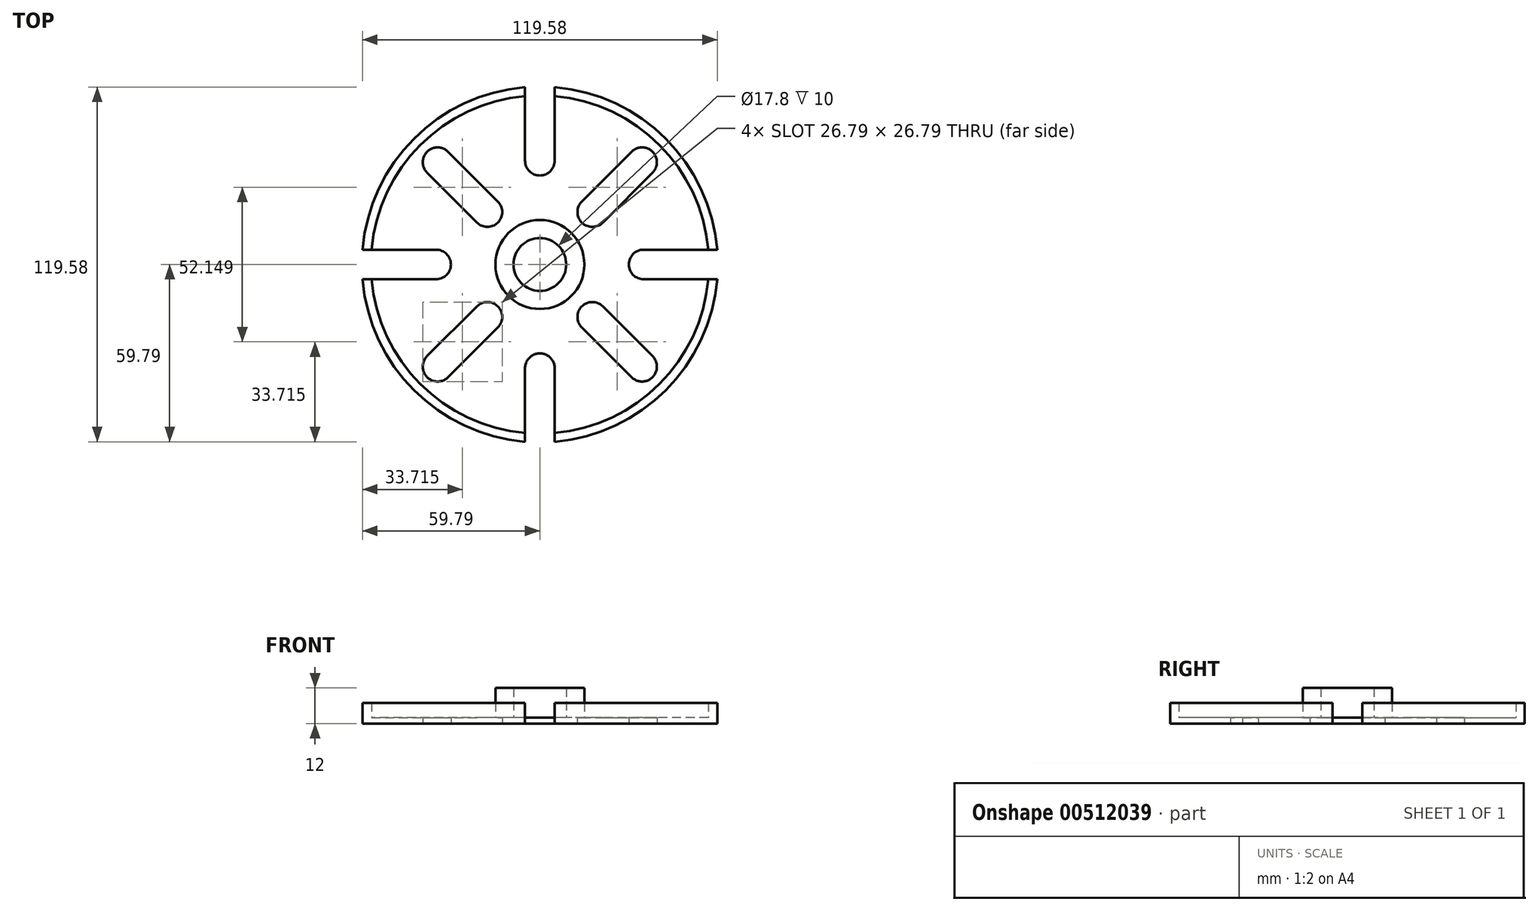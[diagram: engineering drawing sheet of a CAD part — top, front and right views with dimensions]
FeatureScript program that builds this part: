
annotation { "Feature Type Name" : "Feature", "Feature Type Description" : "" }
export const myFeature = defineFeature(function(context is Context, id is Id, definition is map)
    precondition{}
    {
        {
            var Q0;
            Q0=qCreatedBy(makeId("Top.planeOp"),FACE);
            var sketch = newSketch(context, id + "F0", { "sketchPlane" : qUnion([Q0])});
            skCircle(sketch, "E0", {"center": v(0, 0) * mm, "radius": 60 * mm});
            skLineSegment(sketch, "E1", {"start": v(0, 70.03) * mm, "end": v(0, -69.44) * mm, "construction": true});
            skLineSegment(sketch, "E2", {"start": v(57.86, 57.86) * mm, "end": v(-61.51, -61.51) * mm, "construction": true});
            skLineSegment(sketch, "E3", {"start": v(-61.51, 61.51) * mm, "end": v(64.66, -64.66) * mm, "construction": true});
            skCircle(sketch, "E4", {"center": v(0, 0) * mm, "radius": 8.9 * mm});
            skCircle(sketch, "E5", {"center": v(0, 0) * mm, "radius": 15 * mm});
            skLineSegment(sketch, "E6", {"start": v(-59.8, 5) * mm, "end": v(-29.22, 5) * mm});
            skLineSegment(sketch, "E7", {"start": v(52.5, 5) * mm, "end": v(52.5, 0) * mm, "construction": true});
            skLineSegment(sketch, "E8", {"start": v(5, 68.05) * mm, "end": v(0, 68.05) * mm, "construction": true});
            skLineSegment(sketch, "E9", {"start": v(0, 68.05) * mm, "end": v(-5, 68.05) * mm, "construction": true});
            skLineSegment(sketch, "E10", {"start": v(9.76, 16.83) * mm, "end": v(35.2, 42.26) * mm});
            skLineSegment(sketch, "E11", {"start": v(41.96, 34.9) * mm, "end": v(16.3, 9.24) * mm});
            skLineSegment(sketch, "E12", {"start": v(25.46, 32.53) * mm, "end": v(29, 29) * mm, "construction": true});
            skLineSegment(sketch, "E13", {"start": v(29, 29) * mm, "end": v(32.53, 25.46) * mm, "construction": true});
            skLineSegment(sketch, "E14", {"start": v(-35.18, 42.25) * mm, "end": v(-8.95, 16.02) * mm});
            skLineSegment(sketch, "E15", {"start": v(-8.95, 16.02) * mm, "end": v(-12.49, 12.49) * mm, "construction": true});
            skLineSegment(sketch, "E16", {"start": v(-12.49, 12.49) * mm, "end": v(-16.02, 8.95) * mm, "construction": true});
            skLineSegment(sketch, "E17", {"start": v(-16.02, 8.95) * mm, "end": v(-42.44, 35.37) * mm});
            skCircle(sketch, "E18", {"center": v(0, 0) * mm, "radius": 48.75 * mm, "construction": true});
            skCircle(sketch, "E19", {"center": v(-34.47, 34.47) * mm, "radius": 5 * mm});
            skCircle(sketch, "E20", {"center": v(34.47, 34.47) * mm, "radius": 5 * mm});
            skCircle(sketch, "E21", {"center": v(34.47, -34.47) * mm, "radius": 5 * mm});
            skCircle(sketch, "E22", {"center": v(-34.47, -34.47) * mm, "radius": 5 * mm});
            skCircle(sketch, "E23", {"center": v(0, 0) * mm, "radius": 25 * mm, "construction": true});
            skCircle(sketch, "E24", {"center": v(17.68, 17.68) * mm, "radius": 5 * mm});
            skCircle(sketch, "E25", {"center": v(17.68, -17.68) * mm, "radius": 5 * mm});
            skCircle(sketch, "E26", {"center": v(-17.68, -17.68) * mm, "radius": 5 * mm});
            skCircle(sketch, "E27", {"center": v(0, 0) * mm, "radius": 35 * mm, "construction": true});
            skCircle(sketch, "E28", {"center": v(0, 35) * mm, "radius": 5 * mm});
            skCircle(sketch, "E29", {"center": v(35, 0) * mm, "radius": 5 * mm});
            skCircle(sketch, "E30", {"center": v(0, -35) * mm, "radius": 5.01 * mm});
            skCircle(sketch, "E31", {"center": v(-35, 0) * mm, "radius": 5 * mm});
            skCircle(sketch, "E32", {"center": v(-17.68, 17.68) * mm, "radius": 5 * mm});
            skCircle(sketch, "E33", {"center": v(0, 0) * mm, "radius": 57 * mm});
            skLineSegment(sketch, "E34", {"start": v(-59.8, -5) * mm, "end": v(-29.22, -5) * mm});
            skLineSegment(sketch, "E35", {"start": v(59.8, 5) * mm, "end": v(35, 5) * mm});
            skLineSegment(sketch, "E36", {"start": v(59.8, -5) * mm, "end": v(35, -5) * mm});
            skLineSegment(sketch, "E37", {"start": v(52.5, -5) * mm, "end": v(52.5, 0) * mm, "construction": true});
            skLineSegment(sketch, "E38", {"start": v(-38, -30.94) * mm, "end": v(-17.52, -10.45) * mm});
            skLineSegment(sketch, "E39", {"start": v(-8.7, -15.76) * mm, "end": v(-33.57, -40.64) * mm});
            skLineSegment(sketch, "E40", {"start": v(-30.59, -23.52) * mm, "end": v(-27.05, -27.05) * mm, "construction": true});
            skLineSegment(sketch, "E41", {"start": v(-27.05, -27.05) * mm, "end": v(-23.52, -30.59) * mm, "construction": true});
            skLineSegment(sketch, "E42", {"start": v(5, 35) * mm, "end": v(5, 59.8) * mm});
            skLineSegment(sketch, "E43", {"start": v(-5, 35) * mm, "end": v(-5, 59.8) * mm});
            skLineSegment(sketch, "E44", {"start": v(5, -34.64) * mm, "end": v(5, -59.8) * mm});
            skLineSegment(sketch, "E45", {"start": v(-5, -35.36) * mm, "end": v(-5, -59.8) * mm});
            skLineSegment(sketch, "E46", {"start": v(-5, -45.3) * mm, "end": v(0, -45.3) * mm, "construction": true});
            skLineSegment(sketch, "E47", {"start": v(0, -45.3) * mm, "end": v(5, -45.3) * mm, "construction": true});
            skLineSegment(sketch, "E48", {"start": v(16.8, -9.72) * mm, "end": v(41.66, -34.58) * mm});
            skLineSegment(sketch, "E49", {"start": v(10.37, -17.44) * mm, "end": v(33.36, -40.43) * mm});
            skSolve(sketch);
        }
        {
            var Q0;
            {var subQ0=sQuery(id+"F0.wireOp",EDGE,"E35");var subQ1=sQuery(id+"F0.wireOp",EDGE,"E0");var subQ2=makeQuery(id+"F0.imprint","INTERSECT",VERTEX,{"derivedFrom":[subQ1,subQ0]});Q0=makeQuery(id+"F0.imprint","IMPRINT",FACE,{"disambiguationData":[TD([[makeQuery(id+"F0.imprint","IMPRINT",EDGE,{"disambiguationData":[TD([[subQ2,-1.0]])],"derivedFrom":subQ1}),1.0]])]});}
            var Q1;
            {var subQ0=sQuery(id+"F0.wireOp",EDGE,"E6");var subQ1=sQuery(id+"F0.wireOp",EDGE,"E0");var subQ2=makeQuery(id+"F0.imprint","INTERSECT",VERTEX,{"derivedFrom":[subQ1,subQ0]});Q1=makeQuery(id+"F0.imprint","IMPRINT",FACE,{"disambiguationData":[TD([[makeQuery(id+"F0.imprint","IMPRINT",EDGE,{"disambiguationData":[TD([[subQ2,1.0]])],"derivedFrom":subQ1}),1.0]])]});}
            var Q2;
            {var subQ0=sQuery(id+"F0.wireOp",EDGE,"E34");var subQ1=sQuery(id+"F0.wireOp",EDGE,"E0");var subQ2=makeQuery(id+"F0.imprint","INTERSECT",VERTEX,{"derivedFrom":[subQ1,subQ0]});Q2=makeQuery(id+"F0.imprint","IMPRINT",FACE,{"disambiguationData":[TD([[makeQuery(id+"F0.imprint","IMPRINT",EDGE,{"disambiguationData":[TD([[subQ2,-1.0]])],"derivedFrom":subQ1}),1.0]])]});}
            var Q3;
            {var subQ0=sQuery(id+"F0.wireOp",EDGE,"E36");var subQ1=sQuery(id+"F0.wireOp",EDGE,"E0");var subQ2=makeQuery(id+"F0.imprint","INTERSECT",VERTEX,{"derivedFrom":[subQ1,subQ0]});Q3=makeQuery(id+"F0.imprint","IMPRINT",FACE,{"disambiguationData":[TD([[makeQuery(id+"F0.imprint","IMPRINT",EDGE,{"disambiguationData":[TD([[subQ2,1.0]])],"derivedFrom":subQ1}),1.0]])]});}
            extrude(context, id + "F1", {"entities" : qUnion([Q0, Q1, Q2, Q3]), "depth" : 5 * mm, "offsetDistance" : 25 * mm});
        }
        {
            var Q0;
            Q0=makeQuery(id+"F0.imprint","IMPRINT",FACE,{"disambiguationData":[TD([[makeQuery(id+"F0.imprint","IMPRINT",EDGE,{"derivedFrom":sQuery(id+"F0.wireOp",EDGE,"E5")}),-1.0]])]});
            var Q1;
            Q1=makeQuery(id+"F0.imprint","IMPRINT",FACE,{"disambiguationData":[TD([[makeQuery(id+"F0.imprint","IMPRINT",EDGE,{"derivedFrom":sQuery(id+"F0.wireOp",EDGE,"E4")}),-1.0]])]});
            var Q2;
            Q2=makeQuery(id+"F0.imprint","IMPRINT",FACE,{"disambiguationData":[TD([[makeQuery(id+"F0.imprint","IMPRINT",EDGE,{"derivedFrom":sQuery(id+"F0.wireOp",EDGE,"E4")}),1.0]])]});
            var Q3;
            {var subQ0=sQuery(id+"F0.wireOp",EDGE,"E6");var subQ1=sQuery(id+"F0.wireOp",EDGE,"E0");var subQ2=makeQuery(id+"F0.imprint","INTERSECT",VERTEX,{"derivedFrom":[subQ1,subQ0]});Q3=makeQuery(id+"F0.imprint","IMPRINT",FACE,{"disambiguationData":[TD([[makeQuery(id+"F0.imprint","IMPRINT",EDGE,{"disambiguationData":[TD([[subQ2,1.0]])],"derivedFrom":subQ1}),1.0]])]});}
            var Q4;
            Q4=makeQuery(id+"F1.opExtrude","CAP_FACE",FACE,{"disambiguationData":[OSD([sQuery(id+"F0.wireOp",EDGE,"E0"),sQuery(id+"F0.wireOp",EDGE,"E6"),sQuery(id+"F0.wireOp",EDGE,"E33"),sQuery(id+"F0.wireOp",EDGE,"E43")])],"isStart":false});
            var Q5;
            Q5=makeQuery(id+"F1.opExtrude","CAP_FACE",FACE,{"disambiguationData":[OSD([sQuery(id+"F0.wireOp",EDGE,"E0"),sQuery(id+"F0.wireOp",EDGE,"E33"),sQuery(id+"F0.wireOp",EDGE,"E35"),sQuery(id+"F0.wireOp",EDGE,"E42")])],"isStart":false});
            var Q6;
            Q6=makeQuery(id+"F1.opExtrude","CAP_FACE",FACE,{"disambiguationData":[OSD([sQuery(id+"F0.wireOp",EDGE,"E0"),sQuery(id+"F0.wireOp",EDGE,"E33"),sQuery(id+"F0.wireOp",EDGE,"E34"),sQuery(id+"F0.wireOp",EDGE,"E45")])],"isStart":false});
            var Q7;
            Q7=makeQuery(id+"F1.opExtrude","CAP_FACE",FACE,{"disambiguationData":[OSD([sQuery(id+"F0.wireOp",EDGE,"E0"),sQuery(id+"F0.wireOp",EDGE,"E33"),sQuery(id+"F0.wireOp",EDGE,"E36"),sQuery(id+"F0.wireOp",EDGE,"E44")])],"isStart":false});
            extrude(context, id + "F2", {"entities" : qUnion([Q0, Q1, Q2, Q3, Q4, Q5, Q6, Q7]), "operationType" : NewBodyOperationType.ADD, "depth" : 2 * mm, "offsetDistance" : 25 * mm});
        }
        {
            var Q0;
            Q0=makeQuery(id+"F0.imprint","IMPRINT",FACE,{"disambiguationData":[TD([[makeQuery(id+"F0.imprint","IMPRINT",EDGE,{"derivedFrom":sQuery(id+"F0.wireOp",EDGE,"E4")}),-1.0]])]});
            extrude(context, id + "F3", {"entities" : qUnion([Q0]), "operationType" : NewBodyOperationType.ADD, "depth" : 12 * mm, "offsetDistance" : 25 * mm});
        }
    });
